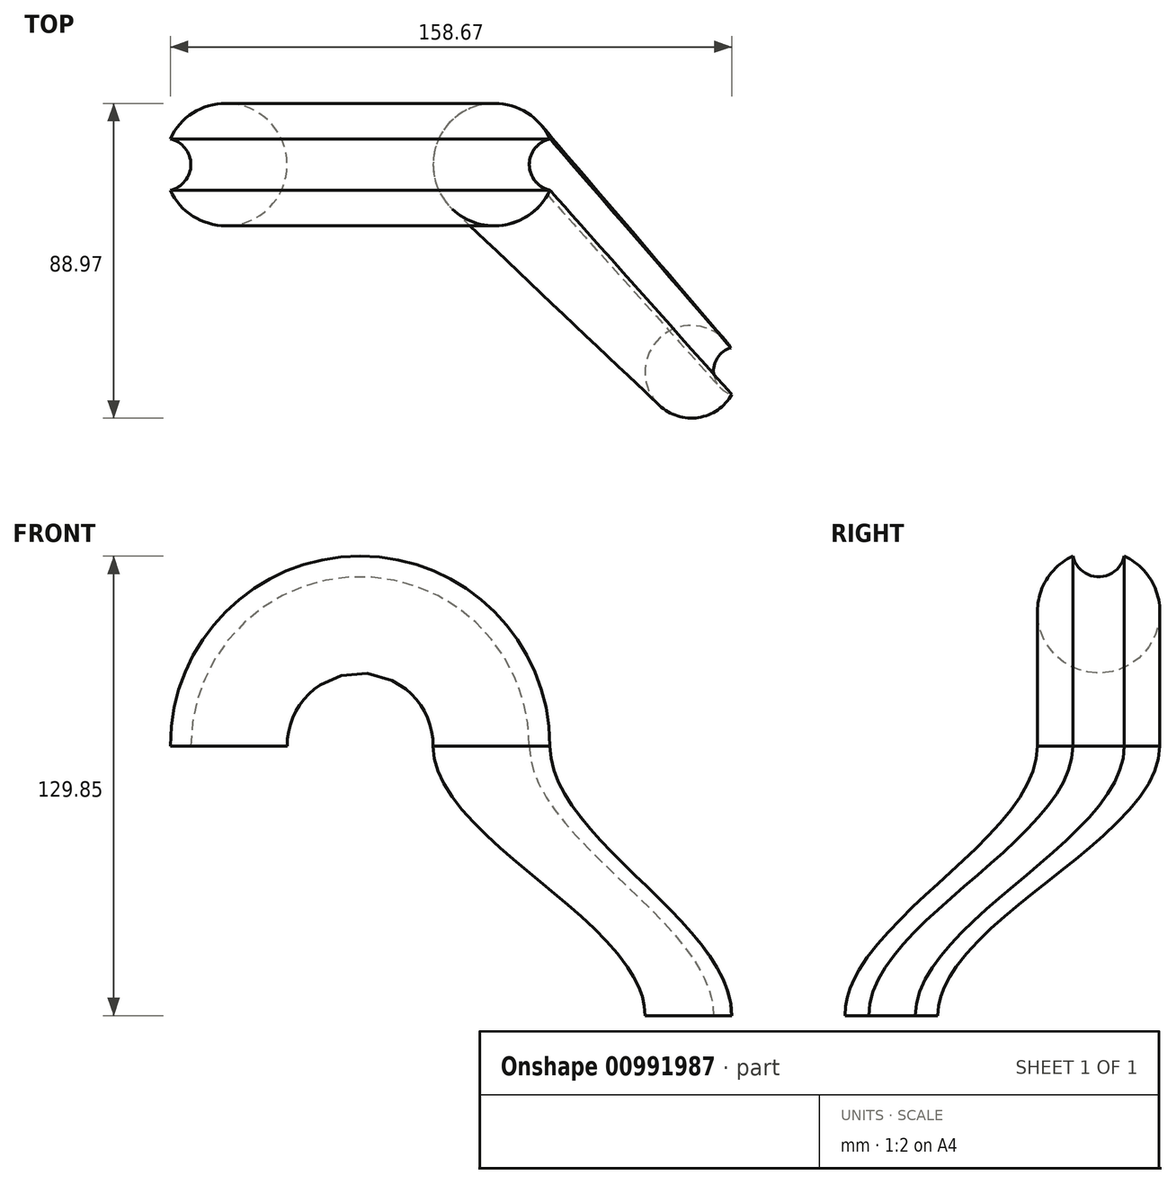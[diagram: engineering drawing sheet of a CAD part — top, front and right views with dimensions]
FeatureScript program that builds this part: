
annotation { "Feature Type Name" : "Feature", "Feature Type Description" : "" }
export const myFeature = defineFeature(function(context is Context, id is Id, definition is map)
    precondition{}
    {
        {
            var Q0;
            Q0=qCreatedBy(makeId("Top.planeOp"),FACE);
            var sketch = newSketch(context, id + "F0", { "sketchPlane" : qUnion([Q0])});
            skArc(sketch, "E0", {"start": v(15.71, 7.25) * mm, "mid": v(-17.3, 0) * mm, "end": v(15.71, -7.25) * mm});
            skArc(sketch, "E1", {"start": v(15.71, 7.25) * mm, "mid": v(9.88, 0) * mm, "end": v(15.71, -7.25) * mm});
            skSolve(sketch);
        }
        {
            var Q0;
            Q0=qCreatedBy(makeId("Front.planeOp"),FACE);
            var sketch = newSketch(context, id + "F1", { "sketchPlane" : qUnion([Q0])});
            skArc(sketch, "E2", {"start": v(0, 0) * mm, "mid": v(-37.93, 37.93) * mm, "end": v(-75.87, 0) * mm});
            skSolve(sketch);
        }
        {
            var Q0;
            Q0=makeQuery(id+"F0.imprint","IMPRINT",FACE,{"disambiguationData":[TD([[makeQuery(id+"F0.imprint","IMPRINT",EDGE,{"derivedFrom":sQuery(id+"F0.wireOp",EDGE,"E0")}),1.0]])]});
            var Q1;
            Q1=sQuery(id+"F1.wireOp",EDGE,"E2");
            sweep(context, id + "F2", {"profiles" : qUnion([Q0]), "path" : qUnion([Q1])});
        }
        {
            var Q0;
            Q0=qCreatedBy(makeId("Top.planeOp"),FACE);
            cPlane(context, id + "F3", {"entities" : qUnion([Q0]), "cplaneType" : CPlaneType.OFFSET, "offset" : 76.2 * mm, "oppositeDirection" : true, "width" : 152.4 * mm, "height" : 152.4 * mm});
        }
        {
            var Q0;
            Q0=qCreatedBy(id+"F3.planeOp",FACE);
            var sketch = newSketch(context, id + "F4", { "sketchPlane" : qUnion([Q0])});
            skArc(sketch, "E3", {"start": v(66.85, -51.8) * mm, "mid": v(42.57, -58.81) * mm, "end": v(67.1, -64.94) * mm});
            skArc(sketch, "E4", {"start": v(66.85, -51.8) * mm, "mid": v(61.93, -58.46) * mm, "end": v(67.1, -64.94) * mm});
            skSolve(sketch);
        }
        {
            var Q0;
            Q0=makeQuery(id+"F4.imprint","IMPRINT",FACE,{"disambiguationData":[TD([[makeQuery(id+"F4.imprint","IMPRINT",EDGE,{"derivedFrom":sQuery(id+"F4.wireOp",EDGE,"E3")}),1.0]])]});
            var Q1;
            Q1=makeQuery(id+"F2.opSweep","CAP_FACE",FACE,{"disambiguationData":[OSD([sQuery(id+"F0.wireOp",EDGE,"E0"),sQuery(id+"F0.wireOp",EDGE,"E1"),sQuery(id+"F1.wireOp",VERTEX,"E2.start")])],"isStart":true});
            loft(context, id + "F5", {"startCondition" : LoftEndDerivativeType.NORMAL_TO_PROFILE, "startMagnitude" : 1, "endCondition" : LoftEndDerivativeType.NORMAL_TO_PROFILE, "endMagnitude" : 1, "sheetProfilesArray" : [{ "sheetProfileEntities" : qUnion([Q0]) }, { "sheetProfileEntities" : qUnion([Q1]) }]});
        }
    });
